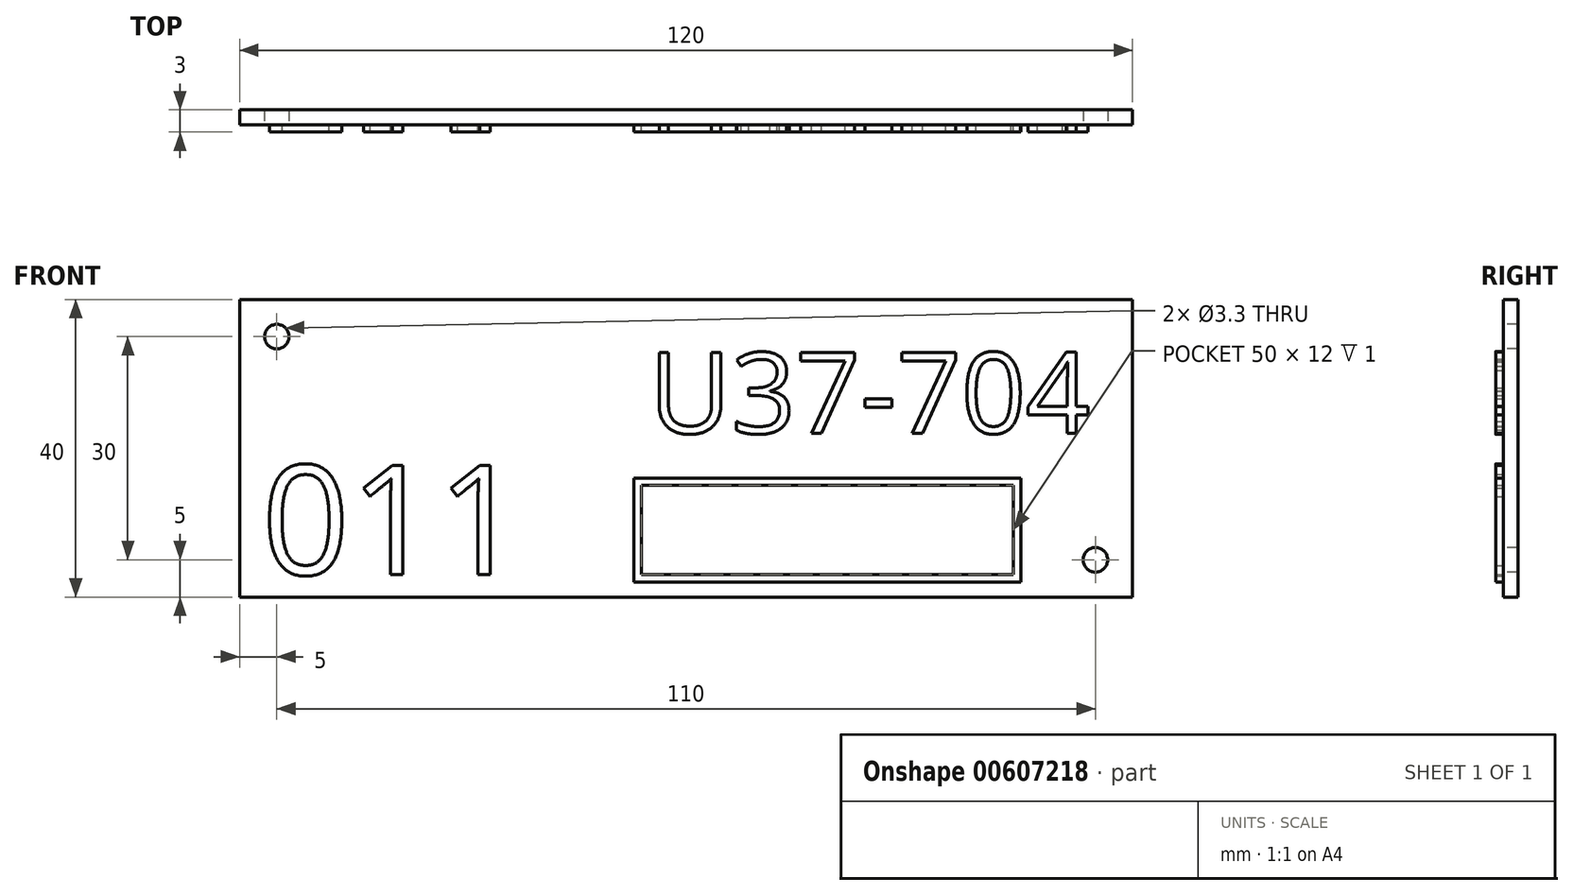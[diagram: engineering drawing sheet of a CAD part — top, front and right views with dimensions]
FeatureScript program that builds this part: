
annotation { "Feature Type Name" : "Feature", "Feature Type Description" : "" }
export const myFeature = defineFeature(function(context is Context, id is Id, definition is map)
    precondition{}
    {
        {
            var Q0;
            Q0=qCreatedBy(makeId("Front.planeOp"),FACE);
            var sketch = newSketch(context, id + "F0", { "sketchPlane" : qUnion([Q0])});
            skLineSegment(sketch, "E0.bottom", {"start": v(60, -20) * mm, "end": v(-60, -20) * mm});
            skLineSegment(sketch, "E0.top", {"start": v(60, 20) * mm, "end": v(-60, 20) * mm});
            skLineSegment(sketch, "E0.left", {"start": v(60, -20) * mm, "end": v(60, 20) * mm});
            skLineSegment(sketch, "E0.right", {"start": v(-60, -20) * mm, "end": v(-60, 20) * mm});
            skPoint(sketch, "E0.middle", {"position": v(0, 0) * mm});
            skSolve(sketch);
        }
        {
            var Q0;
            Q0=makeQuery(id+"F0.imprint","IMPRINT",FACE,{"disambiguationData":[TD([[makeQuery(id+"F0.imprint","IMPRINT",EDGE,{"derivedFrom":sQuery(id+"F0.wireOp",EDGE,"E0.bottom")}),-1.0]])]});
            extrude(context, id + "F1", {"entities" : qUnion([Q0]), "depth" : 2 * mm});
        }
        {
            var Q0;
            Q0=makeQuery(id+"F1.opExtrude","CAP_FACE",FACE,{"disambiguationData":[OSD([sQuery(id+"F0.wireOp",EDGE,"E0.bottom"),sQuery(id+"F0.wireOp",EDGE,"E0.top"),sQuery(id+"F0.wireOp",EDGE,"E0.left"),sQuery(id+"F0.wireOp",EDGE,"E0.right")])],"isStart":false});
            var sketch = newSketch(context, id + "F2", { "sketchPlane" : qUnion([Q0])});
            skPoint(sketch, "E1", {"position": v(-55, 15) * mm});
            skPoint(sketch, "E2", {"position": v(55, -15) * mm});
            skSolve(sketch);
        }
        {
            var Q0;
            Q0=sQuery(id+"F2.wireOp",VERTEX,"E1");
            var Q1;
            Q1=sQuery(id+"F2.wireOp",VERTEX,"E2");
            var Q2;
            Q2=makeQuery(id+"F1.opExtrude","SWEPT_BODY",BODY,{"disambiguationData":[OSD([sQuery(id+"F0.wireOp",EDGE,"E0.bottom"),sQuery(id+"F0.wireOp",EDGE,"E0.top"),sQuery(id+"F0.wireOp",EDGE,"E0.left"),sQuery(id+"F0.wireOp",EDGE,"E0.right")])]});
            hole(context, id + "F3", {"style" : HoleStyle.SIMPLE, "endStyle" : HoleEndStyle.THROUGH, "holeDiameter" : 3.3 * mm, "locations" : qUnion([Q0, Q1]), "scope" : qUnion([Q2]), "isTappedThrough" : true});
        }
        {
            var Q0;
            Q0=makeQuery(id+"F1.opExtrude","CAP_FACE",FACE,{"disambiguationData":[OSD([sQuery(id+"F0.wireOp",EDGE,"E0.bottom"),sQuery(id+"F0.wireOp",EDGE,"E0.top"),sQuery(id+"F0.wireOp",EDGE,"E0.left"),sQuery(id+"F0.wireOp",EDGE,"E0.right")])],"isStart":false});
            var sketch = newSketch(context, id + "F4", { "sketchPlane" : qUnion([Q0])});
            skText(sketch, "E3", { "text": "U37-704", "fontName": "OpenSans-Regular.ttf"});
            const initialGuessF4  = {"E3": [-0.005, 0.002, 1, 0, 0.01093]};
            skSetInitialGuess(sketch, initialGuessF4);
            skSolve(sketch);
        }
        {
            var Q0;
            Q0=qSketchRegion(id+"F4",true);
            extrude(context, id + "F5", {"entities" : qUnion([Q0]), "operationType" : NewBodyOperationType.ADD, "depth" : 1 * mm});
        }
        {
            var Q0;
            {var subQ0=sQuery(id+"F0.wireOp",EDGE,"E0.top");var subQ1=sQuery(id+"F0.wireOp",EDGE,"E0.left");var subQ2=sQuery(id+"F0.wireOp",EDGE,"E0.right");var subQ3=sQuery(id+"F0.wireOp",EDGE,"E0.bottom");Q0=makeQuery(id+"F5.boolean.opBoolean","SPLIT",FACE,{"disambiguationData":[TD([makeQuery(id+"F1.opExtrude","SWEPT_FACE",FACE,{"disambiguationData":[OSD([subQ3])]})])],"derivedFrom":makeQuery(id+"F1.opExtrude","CAP_FACE",FACE,{"disambiguationData":[OSD([subQ3,subQ0,subQ1,subQ2])],"isStart":false})});}
            var sketch = newSketch(context, id + "F6", { "sketchPlane" : qUnion([Q0])});
            skText(sketch, "E4", { "text": "011", "fontName": "OpenSans-Regular.ttf"});
            const initialGuessF6  = {"E4": [-0.057, -0.017, 1, 0, 0.0148]};
            skSetInitialGuess(sketch, initialGuessF6);
            skSolve(sketch);
        }
        {
            var Q0;
            Q0=qSketchRegion(id+"F6",true);
            extrude(context, id + "F7", {"entities" : qUnion([Q0]), "operationType" : NewBodyOperationType.ADD, "depth" : 1 * mm});
        }
        {
            var Q0;
            {var subQ46=sQuery(id+"F0.wireOp",EDGE,"E0.top");var subQ48=sQuery(id+"F0.wireOp",EDGE,"E0.left");var subQ66=sQuery(id+"F0.wireOp",EDGE,"E0.right");var subQ76=sQuery(id+"F0.wireOp",EDGE,"E0.bottom");var subQ77=makeQuery(id+"F1.opExtrude","SWEPT_FACE",FACE,{"disambiguationData":[OSD([subQ76])]});Q0=makeQuery(id+"F7.boolean.opBoolean","SPLIT",FACE,{"disambiguationData":[TD([subQ77])],"derivedFrom":makeQuery(id+"F5.boolean.opBoolean","SPLIT",FACE,{"disambiguationData":[TD([subQ77])],"derivedFrom":makeQuery(id+"F1.opExtrude","CAP_FACE",FACE,{"disambiguationData":[OSD([subQ76,subQ46,subQ48,subQ66])],"isStart":false})})});}
            var sketch = newSketch(context, id + "F8", { "sketchPlane" : qUnion([Q0])});
            skLineSegment(sketch, "E5.bottom", {"start": v(45, -18) * mm, "end": v(-7, -18) * mm});
            skLineSegment(sketch, "E5.top", {"start": v(45, -4) * mm, "end": v(-7, -4) * mm});
            skLineSegment(sketch, "E5.left", {"start": v(45, -18) * mm, "end": v(45, -4) * mm});
            skLineSegment(sketch, "E5.right", {"start": v(-7, -18) * mm, "end": v(-7, -4) * mm});
            skPoint(sketch, "E5.middle", {"position": v(19, -11) * mm});
            skLineSegment(sketch, "E6.0", {"start": v(44, -5) * mm, "end": v(-6, -5) * mm});
            skLineSegment(sketch, "E6.1", {"start": v(44, -17) * mm, "end": v(44, -5) * mm});
            skLineSegment(sketch, "E6.2", {"start": v(44, -17) * mm, "end": v(-6, -17) * mm});
            skLineSegment(sketch, "E6.3", {"start": v(-6, -17) * mm, "end": v(-6, -5) * mm});
            skSolve(sketch);
        }
        {
            var Q0;
            Q0=makeQuery(id+"F8.imprint","IMPRINT",FACE,{"disambiguationData":[TD([[makeQuery(id+"F8.imprint","IMPRINT",EDGE,{"derivedFrom":sQuery(id+"F8.wireOp",EDGE,"E5.bottom")}),-1.0]])]});
            extrude(context, id + "F9", {"entities" : qUnion([Q0]), "operationType" : NewBodyOperationType.ADD, "depth" : 1 * mm});
        }
    });
